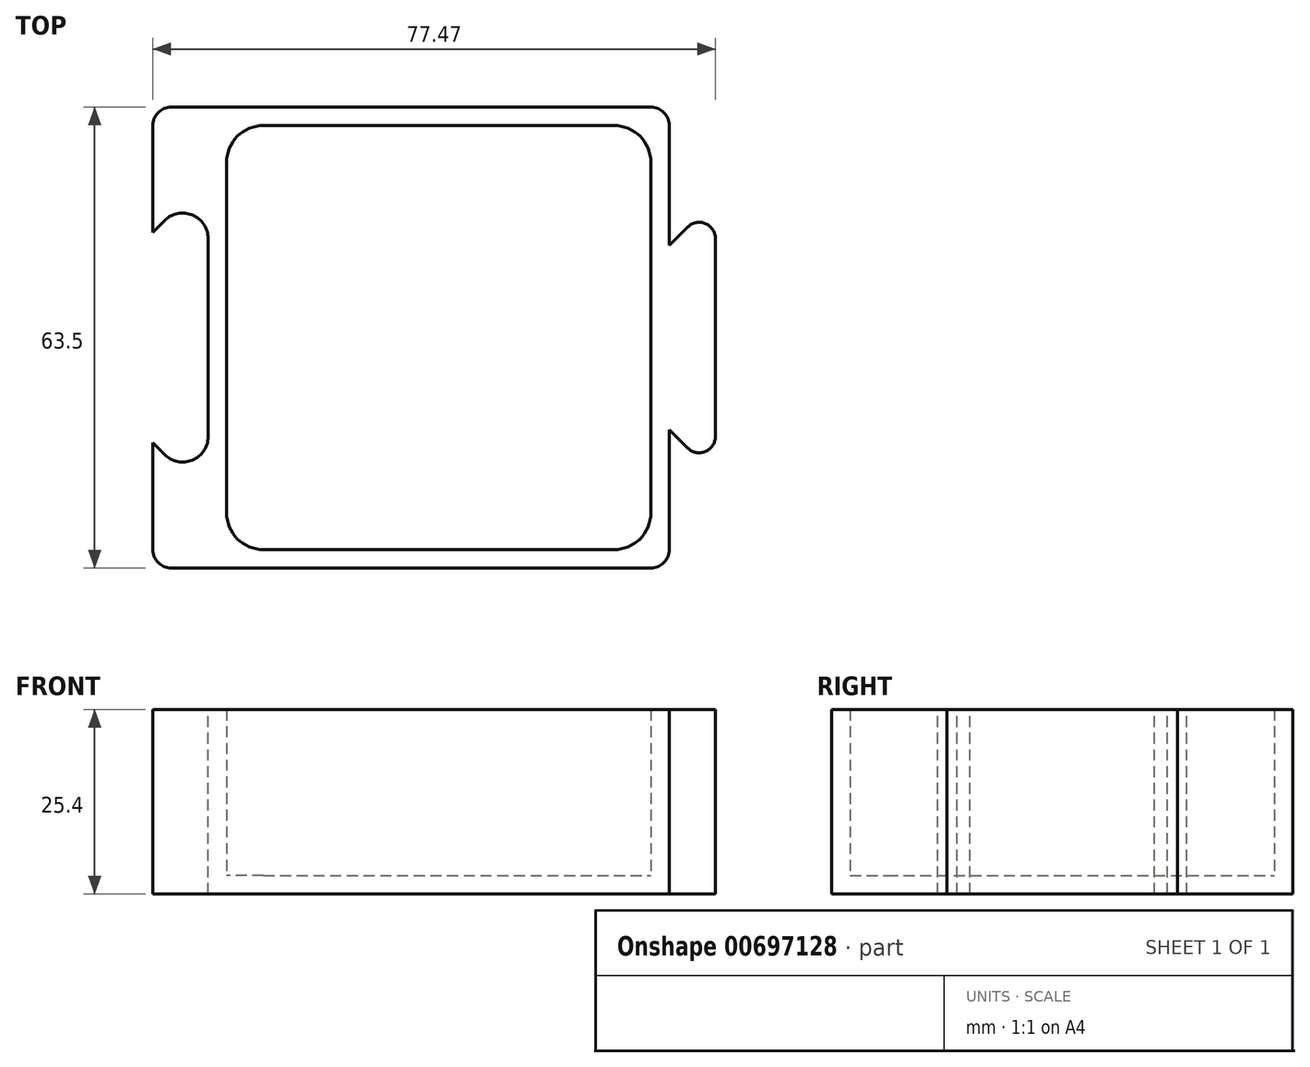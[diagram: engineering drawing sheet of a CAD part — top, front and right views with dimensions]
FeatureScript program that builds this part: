
annotation { "Feature Type Name" : "Feature", "Feature Type Description" : "" }
export const myFeature = defineFeature(function(context is Context, id is Id, definition is map)
    precondition{}
    {
        {
            var Q0;
            Q0=qCreatedBy(makeId("Top.planeOp"),FACE);
            var sketch = newSketch(context, id + "F0", { "sketchPlane" : qUnion([Q0])});
            skLineSegment(sketch, "E0.bottom", {"start": v(0, 0) * mm, "end": v(63.5, 0) * mm});
            skLineSegment(sketch, "E0.top", {"start": v(0, 63.5) * mm, "end": v(63.5, 63.5) * mm});
            skLineSegment(sketch, "E0.left", {"start": v(0, 0) * mm, "end": v(0, 63.5) * mm});
            skLineSegment(sketch, "E0.right", {"start": v(63.5, 0) * mm, "end": v(63.5, 63.5) * mm});
            skSolve(sketch);
        }
        {
            var Q0;
            Q0 = qSketchRegion(id + "F0", true);
            extrude(context, id + "F1", {"entities" : qUnion([Q0]), "depth" : 25.4 * mm, "offsetDistance" : 25.4 * mm});
        }
        {
            var Q0;
            Q0=makeQuery(id+"F1.opExtrude","CAP_FACE",FACE,{"disambiguationData":[OSD([sQuery(id+"F0.wireOp",EDGE,"E0.bottom"),sQuery(id+"F0.wireOp",EDGE,"E0.top"),sQuery(id+"F0.wireOp",EDGE,"E0.left"),sQuery(id+"F0.wireOp",EDGE,"E0.right")])],"isStart":false});
            shell(context, id + "F2", {"entities" : qUnion([Q0]), "thickness" : 2.54 * mm});
        }
        {
            var Q0;
            Q0=makeQuery(id+"F1.opExtrude","CAP_FACE",FACE,{"disambiguationData":[OSD([sQuery(id+"F0.wireOp",EDGE,"E0.bottom"),sQuery(id+"F0.wireOp",EDGE,"E0.top"),sQuery(id+"F0.wireOp",EDGE,"E0.left"),sQuery(id+"F0.wireOp",EDGE,"E0.right")])],"isStart":false});
            var sketch = newSketch(context, id + "F3", { "sketchPlane" : qUnion([Q0])});
            skLineSegment(sketch, "E1", {"start": v(63.5, 44.45) * mm, "end": v(66.02, 46.97) * mm});
            skArc(sketch, "E2", {"start": v(69.85, 45.38) * mm, "mid": v(68.46, 47.45) * mm, "end": v(66.02, 46.97) * mm});
            skLineSegment(sketch, "E3", {"start": v(69.85, 45.38) * mm, "end": v(69.85, 18.12) * mm});
            skArc(sketch, "E4", {"start": v(66.02, 16.53) * mm, "mid": v(68.46, 16.05) * mm, "end": v(69.85, 18.12) * mm});
            skLineSegment(sketch, "E5", {"start": v(66.02, 16.53) * mm, "end": v(63.5, 19.05) * mm});
            skLineSegment(sketch, "E6", {"start": v(63.5, 19.05) * mm, "end": v(63.5, 44.45) * mm});
            skLineSegment(sketch, "E7", {"start": v(0, 31.75) * mm, "end": v(63.5, 31.75) * mm, "construction": true});
            skLineSegment(sketch, "E8", {"start": v(69.85, 31.75) * mm, "end": v(63.5, 31.75) * mm, "construction": true});
            skLineSegment(sketch, "E9", {"start": v(31.75, 63.5) * mm, "end": v(31.75, 0) * mm, "construction": true});
            skArc(sketch, "E10.1.0.0", {"start": v(-1.27, 45.38) * mm, "mid": v(-2.66, 47.45) * mm, "end": v(-5.1, 46.97) * mm, "construction": true});
            skLineSegment(sketch, "E10.1.0.1", {"start": v(-1.27, 31.75) * mm, "end": v(-7.62, 31.75) * mm, "construction": true});
            skLineSegment(sketch, "E10.1.0.2", {"start": v(-7.62, 19.05) * mm, "end": v(-7.62, 44.45) * mm, "construction": true});
            skLineSegment(sketch, "E10.1.0.3", {"start": v(-5.1, 16.53) * mm, "end": v(-7.62, 19.05) * mm, "construction": true});
            skArc(sketch, "E10.1.0.4", {"start": v(-5.1, 16.53) * mm, "mid": v(-2.66, 16.05) * mm, "end": v(-1.27, 18.12) * mm, "construction": true});
            skLineSegment(sketch, "E10.1.0.5", {"start": v(-1.27, 45.38) * mm, "end": v(-1.27, 18.12) * mm, "construction": true});
            skLineSegment(sketch, "E10.1.0.6", {"start": v(-7.62, 44.45) * mm, "end": v(-5.1, 46.97) * mm, "construction": true});
            skLineSegment(sketch, "E10.direction1", {"start": v(66.02, 16.53) * mm, "end": v(-5.1, 16.53) * mm, "construction": true});
            skLineSegment(sketch, "E11", {"start": v(0, 63.5) * mm, "end": v(-7.62, 63.5) * mm});
            skLineSegment(sketch, "E12", {"start": v(-7.62, 63.5) * mm, "end": v(-7.62, 46.25) * mm});
            skLineSegment(sketch, "E13", {"start": v(-7.62, 46.25) * mm, "end": v(-6, 47.87) * mm});
            skArc(sketch, "E14", {"start": v(0, 45.38) * mm, "mid": v(-2.17, 48.63) * mm, "end": v(-6, 47.87) * mm});
            skLineSegment(sketch, "E15", {"start": v(0, 63.5) * mm, "end": v(0, 45.38) * mm});
            skLineSegment(sketch, "E16.MirrorCS", {"start": v(-7.62, 17.25) * mm, "end": v(-6, 15.63) * mm});
            skLineSegment(sketch, "E17.MirrorCS", {"start": v(0, 0) * mm, "end": v(0, 18.12) * mm});
            skArc(sketch, "E18.MirrorCS", {"start": v(0, 18.12) * mm, "mid": v(-2.17, 14.87) * mm, "end": v(-6, 15.63) * mm});
            skLineSegment(sketch, "E19.MirrorCS", {"start": v(-7.62, 0) * mm, "end": v(-7.62, 17.25) * mm});
            skLineSegment(sketch, "E20.MirrorCS", {"start": v(0, 0) * mm, "end": v(-7.62, 0) * mm});
            skArc(sketch, "E21.MirrorCS", {"start": v(-1.27, 18.12) * mm, "mid": v(-2.66, 16.05) * mm, "end": v(-5.1, 16.53) * mm, "construction": true});
            skSolve(sketch);
        }
        {
            var Q0;
            Q0 = qSketchRegion(id + "F3", true);
            var Q1;
            Q1=makeQuery(id+"F1.opExtrude","CAP_FACE",FACE,{"disambiguationData":[OSD([sQuery(id+"F0.wireOp",EDGE,"E0.bottom"),sQuery(id+"F0.wireOp",EDGE,"E0.top"),sQuery(id+"F0.wireOp",EDGE,"E0.left"),sQuery(id+"F0.wireOp",EDGE,"E0.right")])],"isStart":true});
            extrude(context, id + "F4", {"entities" : qUnion([Q0]), "operationType" : NewBodyOperationType.ADD, "endBound" : BoundingType.UP_TO_SURFACE, "oppositeDirection" : true, "depth" : 25.4 * mm, "endBoundEntityFace" : qUnion([Q1]), "offsetDistance" : 25.4 * mm});
        }
        {
            var Q0;
            Q0=makeQuery(id+"F2.opShell","OFFSET_EDGE",EDGE,{"disambiguationData":[OSD([sQuery(id+"F0.wireOp",EDGE,"E0.top"),sQuery(id+"F0.wireOp",EDGE,"E0.left")])]});
            var Q1;
            Q1=makeQuery(id+"F2.opShell","OFFSET_EDGE",EDGE,{"disambiguationData":[OSD([sQuery(id+"F0.wireOp",EDGE,"E0.top"),sQuery(id+"F0.wireOp",EDGE,"E0.right")])]});
            var Q2;
            Q2=makeQuery(id+"F2.opShell","OFFSET_EDGE",EDGE,{"disambiguationData":[OSD([sQuery(id+"F0.wireOp",EDGE,"E0.bottom"),sQuery(id+"F0.wireOp",EDGE,"E0.left")])]});
            var Q3;
            Q3=makeQuery(id+"F2.opShell","OFFSET_EDGE",EDGE,{"disambiguationData":[OSD([sQuery(id+"F0.wireOp",EDGE,"E0.bottom"),sQuery(id+"F0.wireOp",EDGE,"E0.right")])]});
            fillet(context, id + "F5", {"entities" : qUnion([Q0, Q1, Q2, Q3]), "radius" : 5.08 * mm, "tangentPropagation" : true, "allowEdgeOverflow" : false});
        }
        {
            var Q0;
            Q0=makeQuery(id+"F4.opExtrude","SWEPT_EDGE",EDGE,{"disambiguationData":[OSD([sQuery(id+"F3.wireOp",EDGE,"E11"),sQuery(id+"F3.wireOp",EDGE,"E12")])]});
            var Q1;
            Q1=makeQuery(id+"F1.opExtrude","SWEPT_EDGE",EDGE,{"disambiguationData":[OSD([sQuery(id+"F0.wireOp",EDGE,"E0.top"),sQuery(id+"F0.wireOp",EDGE,"E0.right")])]});
            var Q2;
            Q2=makeQuery(id+"F1.opExtrude","SWEPT_EDGE",EDGE,{"disambiguationData":[OSD([sQuery(id+"F0.wireOp",EDGE,"E0.bottom"),sQuery(id+"F0.wireOp",EDGE,"E0.right")])]});
            var Q3;
            Q3=makeQuery(id+"F4.opExtrude","SWEPT_EDGE",EDGE,{"disambiguationData":[OSD([sQuery(id+"F3.wireOp",EDGE,"E19.MirrorCS"),sQuery(id+"F3.wireOp",EDGE,"E20.MirrorCS")])]});
            fillet(context, id + "F6", {"entities" : qUnion([Q0, Q1, Q2, Q3]), "radius" : 2.54 * mm, "tangentPropagation" : true, "allowEdgeOverflow" : false});
        }
    });
